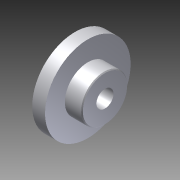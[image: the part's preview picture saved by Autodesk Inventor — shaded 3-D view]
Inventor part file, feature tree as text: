
AUTODESK INVENTOR PART (.ipt)
format: ipt  version: 2012 (Build 160160000, 160)  size: 641,536 bytes
history: native  units: in
note: dims shown in document units (in); Inventor stores cm internally (conversion verified against a paired STEP export)
features: extrude x3, sketch x1, chamfer x1, imported_body x1
ambient origin geometry x8: Origin, YZ Plane, XZ Plane, XY Plane, X Axis, Y Axis, Z Axis, Center Point
feature tree (6):
  sketch  "Sketch1"  dims[d0=0.25in d1=0.5625in d2=0.0in d3=1.25in d4=1.0in d5=0.0in d6=0.125in d7=0.0in d8=0.0125in d9=0.125in d10=45.0deg]
  extrude  "Extrusion1"  Depth=0.5625in TaperAngle=0.0deg
  extrude  "Extrusion2"  Depth=1.25in
  extrude  "Extrusion3"  Depth=1.0in TaperAngle=0.0deg
  chamfer  "Chamfer1"  Distance=0.125in
  imported_body  "Base1"
